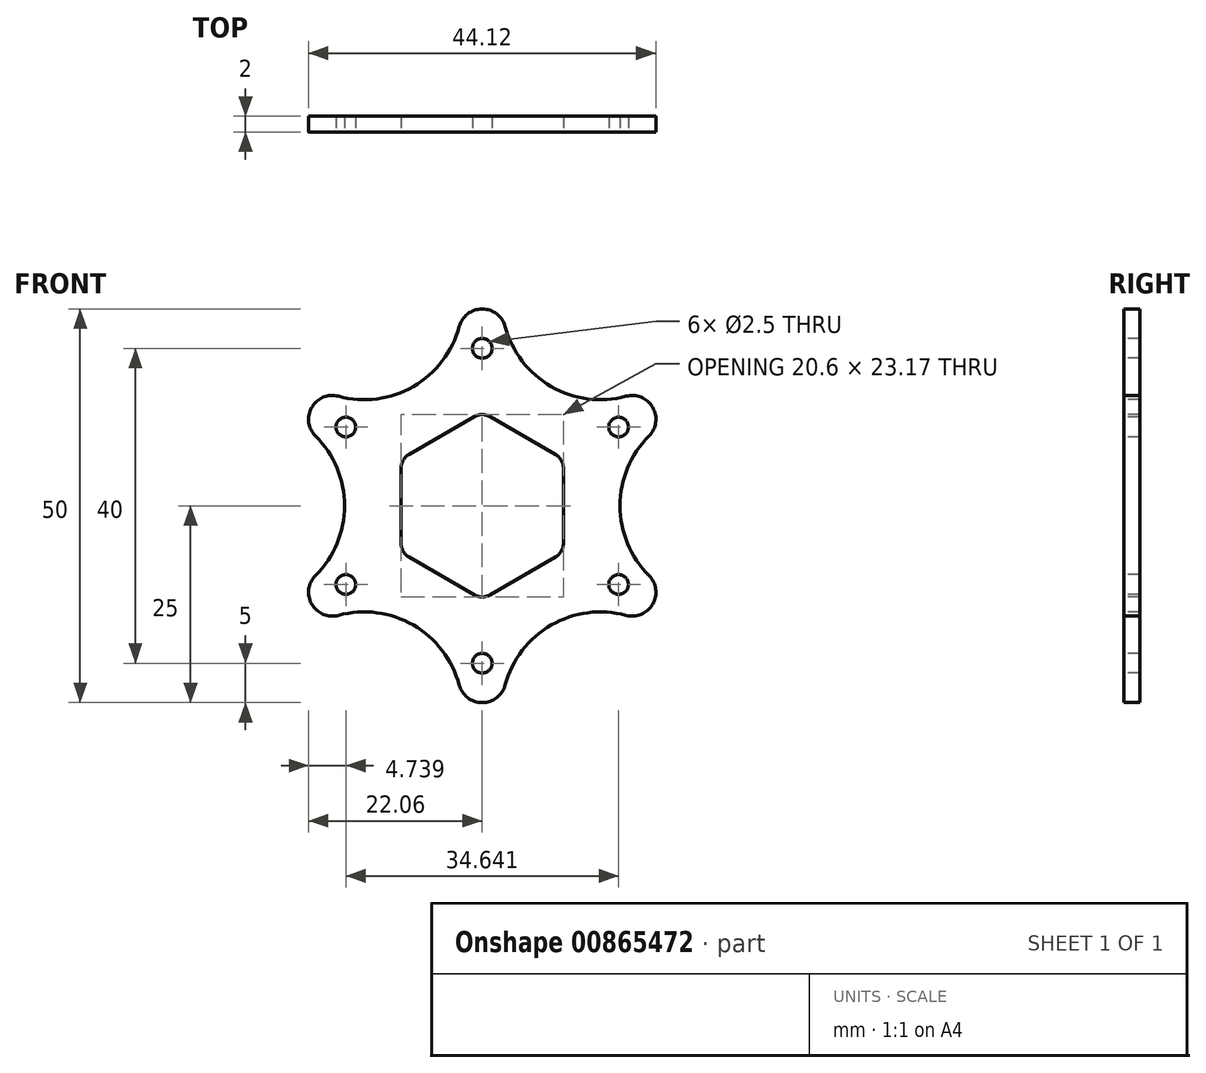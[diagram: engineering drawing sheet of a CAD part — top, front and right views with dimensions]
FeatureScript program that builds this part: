
annotation { "Feature Type Name" : "Feature", "Feature Type Description" : "" }
export const myFeature = defineFeature(function(context is Context, id is Id, definition is map)
    precondition{}
    {
        {
            var Q0;
            Q0=qCreatedBy(makeId("Front.planeOp"),FACE);
            var sketch = newSketch(context, id + "F0", { "sketchPlane" : qUnion([Q0])});
            skPoint(sketch, "E0.middle", {"position": v(0, 0) * mm});
            skPoint(sketch, "E1.center.orphan", {"position": v(-16.73, 20.91) * mm});
            skPoint(sketch, "E0.left.start.orphan", {"position": v(20.91, 25.1) * mm});
            skPoint(sketch, "E0.right.start.orphan", {"position": v(-20.91, 25.1) * mm});
            skPoint(sketch, "E0.top.end.orphan", {"position": v(-20.91, -25.1) * mm});
            skPoint(sketch, "E0.top.start.orphan", {"position": v(20.91, -25.1) * mm});
            skPoint(sketch, "E2.center.orphan", {"position": v(-16.73, -20.91) * mm});
            skPoint(sketch, "E3.center.orphan", {"position": v(16.73, -20.91) * mm});
            skCircle(sketch, "E4", {"center": v(0, 0) * mm, "radius": 25 * mm});
            skSolve(sketch);
        }
        {
            var Q0;
            Q0=qSketchRegion(id+"F0",true);
            extrude(context, id + "F1", {"entities" : qUnion([Q0]), "depth" : 2 * mm, "offsetDistance" : 25 * mm});
        }
        {
            var Q0;
            Q0=makeQuery(id+"F1.opExtrude","CAP_FACE",FACE,{"disambiguationData":[OSD([sQuery(id+"F0.wireOp",EDGE,"E4")])],"isStart":false});
            var sketch = newSketch(context, id + "F2", { "sketchPlane" : qUnion([Q0])});
            skCircle(sketch, "E5.cCircle", {"center": v(0, 0) * mm, "radius": 10.3 * mm, "construction": true});
            skLineSegment(sketch, "E5.0", {"start": v(-9.3, 6.52) * mm, "end": v(-1, 11.32) * mm});
            skLineSegment(sketch, "E5.1", {"start": v(1, 11.32) * mm, "end": v(9.3, 6.52) * mm});
            skLineSegment(sketch, "E5.2", {"start": v(10.3, 4.8) * mm, "end": v(10.3, -4.8) * mm});
            skLineSegment(sketch, "E5.3", {"start": v(9.3, -6.52) * mm, "end": v(1, -11.32) * mm});
            skLineSegment(sketch, "E5.4", {"start": v(-1, -11.32) * mm, "end": v(-9.3, -6.52) * mm});
            skLineSegment(sketch, "E5.5", {"start": v(-10.3, -4.8) * mm, "end": v(-10.3, 4.8) * mm});
            skPoint(sketch, "E5.0.midPoint", {"position": v(-5.15, 8.92) * mm});
            skPoint(sketch, "E6.visualSharp", {"position": v(0, -11.9) * mm});
            skArc(sketch, "E6.filletArc", {"start": v(-1, -11.32) * mm, "mid": v(0, -11.58) * mm, "end": v(1, -11.32) * mm});
            skPoint(sketch, "E7.visualSharp", {"position": v(-10.3, -5.95) * mm});
            skArc(sketch, "E7.filletArc", {"start": v(-10.3, -4.8) * mm, "mid": v(-10.03, -5.8) * mm, "end": v(-9.3, -6.52) * mm});
            skPoint(sketch, "E8.visualSharp", {"position": v(-10.3, 5.95) * mm});
            skArc(sketch, "E8.filletArc", {"start": v(-9.3, 6.52) * mm, "mid": v(-10.03, 5.8) * mm, "end": v(-10.3, 4.8) * mm});
            skPoint(sketch, "E9.visualSharp", {"position": v(0, 11.9) * mm});
            skArc(sketch, "E9.filletArc", {"start": v(1, 11.32) * mm, "mid": v(0, 11.58) * mm, "end": v(-1, 11.32) * mm});
            skPoint(sketch, "E10.visualSharp", {"position": v(10.3, 5.95) * mm});
            skArc(sketch, "E10.filletArc", {"start": v(10.3, 4.8) * mm, "mid": v(10.03, 5.8) * mm, "end": v(9.3, 6.52) * mm});
            skPoint(sketch, "E11.visualSharp", {"position": v(10.3, -5.95) * mm});
            skArc(sketch, "E11.filletArc", {"start": v(9.3, -6.52) * mm, "mid": v(10.03, -5.8) * mm, "end": v(10.3, -4.8) * mm});
            skLineSegment(sketch, "E12", {"start": v(0, 0.35) * mm, "end": v(22.67, 0.35) * mm});
            skLineSegment(sketch, "E13", {"start": v(0, 0) * mm, "end": v(0, 11.9) * mm});
            skSolve(sketch);
        }
        {
            var Q0;
            Q0 = qSketchRegion(id + "F2", true);
            extrude(context, id + "F3", {"entities" : qUnion([Q0]), "operationType" : NewBodyOperationType.REMOVE, "endBound" : BoundingType.THROUGH_ALL, "oppositeDirection" : true, "depth" : 25 * mm, "offsetDistance" : 25 * mm});
        }
        {
            var Q0;
            Q0=makeQuery(id+"F1.opExtrude","CAP_FACE",FACE,{"disambiguationData":[OSD([sQuery(id+"F0.wireOp",EDGE,"E4")])],"isStart":false});
            var sketch = newSketch(context, id + "F4", { "sketchPlane" : qUnion([Q0])});
            skCircle(sketch, "E14", {"center": v(0, 20) * mm, "radius": 1.25 * mm});
            skCircle(sketch, "E15.1.0", {"center": v(-17.32, 10) * mm, "radius": 1.25 * mm});
            skCircle(sketch, "E15.2.0", {"center": v(-17.32, -10) * mm, "radius": 1.25 * mm});
            skCircle(sketch, "E15.3.0", {"center": v(0, -20) * mm, "radius": 1.25 * mm});
            skCircle(sketch, "E15.4.0", {"center": v(17.32, -10) * mm, "radius": 1.25 * mm});
            skCircle(sketch, "E15.5.0", {"center": v(17.32, 10) * mm, "radius": 1.25 * mm});
            skPoint(sketch, "E15.center", {"position": v(0, 0) * mm});
            skSolve(sketch);
        }
        {
            var Q0;
            Q0 = qSketchRegion(id + "F4", true);
            extrude(context, id + "F5", {"entities" : qUnion([Q0]), "operationType" : NewBodyOperationType.REMOVE, "endBound" : BoundingType.THROUGH_ALL, "oppositeDirection" : true, "depth" : 25 * mm, "offsetDistance" : 25 * mm});
        }
        {
            var Q0;
            Q0=makeQuery(id+"F1.opExtrude","CAP_FACE",FACE,{"disambiguationData":[OSD([sQuery(id+"F0.wireOp",EDGE,"E4")])],"isStart":false});
            var sketch = newSketch(context, id + "F6", { "sketchPlane" : qUnion([Q0])});
            skCircle(sketch, "E16", {"center": v(30, 0) * mm, "radius": 12.5 * mm});
            skCircle(sketch, "E17.1.0", {"center": v(15, 25.98) * mm, "radius": 12.5 * mm});
            skCircle(sketch, "E17.2.0", {"center": v(-15, 25.98) * mm, "radius": 12.5 * mm});
            skCircle(sketch, "E17.3.0", {"center": v(-30, 0) * mm, "radius": 12.5 * mm});
            skCircle(sketch, "E17.4.0", {"center": v(-15, -25.98) * mm, "radius": 12.5 * mm});
            skCircle(sketch, "E17.5.0", {"center": v(15, -25.98) * mm, "radius": 12.5 * mm});
            skPoint(sketch, "E17.center", {"position": v(0, 0) * mm});
            skLineSegment(sketch, "E18", {"start": v(0, 0) * mm, "end": v(-36.1, 36.1) * mm});
            skLineSegment(sketch, "E19", {"start": v(0, 0) * mm, "end": v(30, 0) * mm});
            skSolve(sketch);
        }
        {
            var Q0;
            Q0 = qSketchRegion(id + "F6", true);
            extrude(context, id + "F7", {"entities" : qUnion([Q0]), "operationType" : NewBodyOperationType.REMOVE, "endBound" : BoundingType.THROUGH_ALL, "oppositeDirection" : true, "depth" : 25 * mm, "offsetDistance" : 25 * mm});
        }
        {
            var Q0;
            Q0=makeQuery(id+"F7.boolean.opBoolean","INTERSECT",EDGE,{"disambiguationData":[OD(0.0)],"derivedFrom":[makeQuery(id+"F1.opExtrude","SWEPT_FACE",FACE,{"disambiguationData":[OSD([sQuery(id+"F0.wireOp",EDGE,"E4")])]}),makeQuery(id+"F7.opExtrude","SWEPT_FACE",FACE,{"disambiguationData":[OSD([sQuery(id+"F6.wireOp",EDGE,"E16")])]})]});
            var Q1;
            Q1=makeQuery(id+"F7.boolean.opBoolean","INTERSECT",EDGE,{"disambiguationData":[OD(0.0)],"derivedFrom":[makeQuery(id+"F1.opExtrude","SWEPT_FACE",FACE,{"disambiguationData":[OSD([sQuery(id+"F0.wireOp",EDGE,"E4")])]}),makeQuery(id+"F7.opExtrude","SWEPT_FACE",FACE,{"disambiguationData":[OSD([sQuery(id+"F6.wireOp",EDGE,"E17.1.0")])]})]});
            var Q2;
            Q2=makeQuery(id+"F7.boolean.opBoolean","INTERSECT",EDGE,{"disambiguationData":[OD(1.0)],"derivedFrom":[makeQuery(id+"F1.opExtrude","SWEPT_FACE",FACE,{"disambiguationData":[OSD([sQuery(id+"F0.wireOp",EDGE,"E4")])]}),makeQuery(id+"F7.opExtrude","SWEPT_FACE",FACE,{"disambiguationData":[OSD([sQuery(id+"F6.wireOp",EDGE,"E16")])]})]});
            var Q3;
            Q3=makeQuery(id+"F7.boolean.opBoolean","INTERSECT",EDGE,{"disambiguationData":[OD(0.0)],"derivedFrom":[makeQuery(id+"F1.opExtrude","SWEPT_FACE",FACE,{"disambiguationData":[OSD([sQuery(id+"F0.wireOp",EDGE,"E4")])]}),makeQuery(id+"F7.opExtrude","SWEPT_FACE",FACE,{"disambiguationData":[OSD([sQuery(id+"F6.wireOp",EDGE,"E17.5.0")])]})]});
            var Q4;
            Q4=makeQuery(id+"F7.boolean.opBoolean","INTERSECT",EDGE,{"disambiguationData":[OD(1.0)],"derivedFrom":[makeQuery(id+"F1.opExtrude","SWEPT_FACE",FACE,{"disambiguationData":[OSD([sQuery(id+"F0.wireOp",EDGE,"E4")])]}),makeQuery(id+"F7.opExtrude","SWEPT_FACE",FACE,{"disambiguationData":[OSD([sQuery(id+"F6.wireOp",EDGE,"E17.5.0")])]})]});
            var Q5;
            Q5=makeQuery(id+"F7.boolean.opBoolean","INTERSECT",EDGE,{"disambiguationData":[OD(1.0)],"derivedFrom":[makeQuery(id+"F1.opExtrude","SWEPT_FACE",FACE,{"disambiguationData":[OSD([sQuery(id+"F0.wireOp",EDGE,"E4")])]}),makeQuery(id+"F7.opExtrude","SWEPT_FACE",FACE,{"disambiguationData":[OSD([sQuery(id+"F6.wireOp",EDGE,"E17.4.0")])]})]});
            var Q6;
            Q6=makeQuery(id+"F7.boolean.opBoolean","INTERSECT",EDGE,{"disambiguationData":[OD(0.0)],"derivedFrom":[makeQuery(id+"F1.opExtrude","SWEPT_FACE",FACE,{"disambiguationData":[OSD([sQuery(id+"F0.wireOp",EDGE,"E4")])]}),makeQuery(id+"F7.opExtrude","SWEPT_FACE",FACE,{"disambiguationData":[OSD([sQuery(id+"F6.wireOp",EDGE,"E17.4.0")])]})]});
            var Q7;
            Q7=makeQuery(id+"F7.boolean.opBoolean","INTERSECT",EDGE,{"disambiguationData":[OD(1.0)],"derivedFrom":[makeQuery(id+"F1.opExtrude","SWEPT_FACE",FACE,{"disambiguationData":[OSD([sQuery(id+"F0.wireOp",EDGE,"E4")])]}),makeQuery(id+"F7.opExtrude","SWEPT_FACE",FACE,{"disambiguationData":[OSD([sQuery(id+"F6.wireOp",EDGE,"E17.3.0")])]})]});
            var Q8;
            Q8=makeQuery(id+"F7.boolean.opBoolean","INTERSECT",EDGE,{"disambiguationData":[OD(0.0)],"derivedFrom":[makeQuery(id+"F1.opExtrude","SWEPT_FACE",FACE,{"disambiguationData":[OSD([sQuery(id+"F0.wireOp",EDGE,"E4")])]}),makeQuery(id+"F7.opExtrude","SWEPT_FACE",FACE,{"disambiguationData":[OSD([sQuery(id+"F6.wireOp",EDGE,"E17.3.0")])]})]});
            var Q9;
            Q9=makeQuery(id+"F7.boolean.opBoolean","INTERSECT",EDGE,{"disambiguationData":[OD(1.0)],"derivedFrom":[makeQuery(id+"F1.opExtrude","SWEPT_FACE",FACE,{"disambiguationData":[OSD([sQuery(id+"F0.wireOp",EDGE,"E4")])]}),makeQuery(id+"F7.opExtrude","SWEPT_FACE",FACE,{"disambiguationData":[OSD([sQuery(id+"F6.wireOp",EDGE,"E17.2.0")])]})]});
            var Q10;
            Q10=makeQuery(id+"F7.boolean.opBoolean","INTERSECT",EDGE,{"disambiguationData":[OD(0.0)],"derivedFrom":[makeQuery(id+"F1.opExtrude","SWEPT_FACE",FACE,{"disambiguationData":[OSD([sQuery(id+"F0.wireOp",EDGE,"E4")])]}),makeQuery(id+"F7.opExtrude","SWEPT_FACE",FACE,{"disambiguationData":[OSD([sQuery(id+"F6.wireOp",EDGE,"E17.2.0")])]})]});
            var Q11;
            Q11=makeQuery(id+"F7.boolean.opBoolean","INTERSECT",EDGE,{"disambiguationData":[OD(1.0)],"derivedFrom":[makeQuery(id+"F1.opExtrude","SWEPT_FACE",FACE,{"disambiguationData":[OSD([sQuery(id+"F0.wireOp",EDGE,"E4")])]}),makeQuery(id+"F7.opExtrude","SWEPT_FACE",FACE,{"disambiguationData":[OSD([sQuery(id+"F6.wireOp",EDGE,"E17.1.0")])]})]});
            fillet(context, id + "F8", {"entities" : qUnion([Q0, Q1, Q2, Q3, Q4, Q5, Q6, Q7, Q8, Q9, Q10, Q11]), "radius" : 3 * mm, "tangentPropagation" : true, "allowEdgeOverflow" : false});
        }
    });
